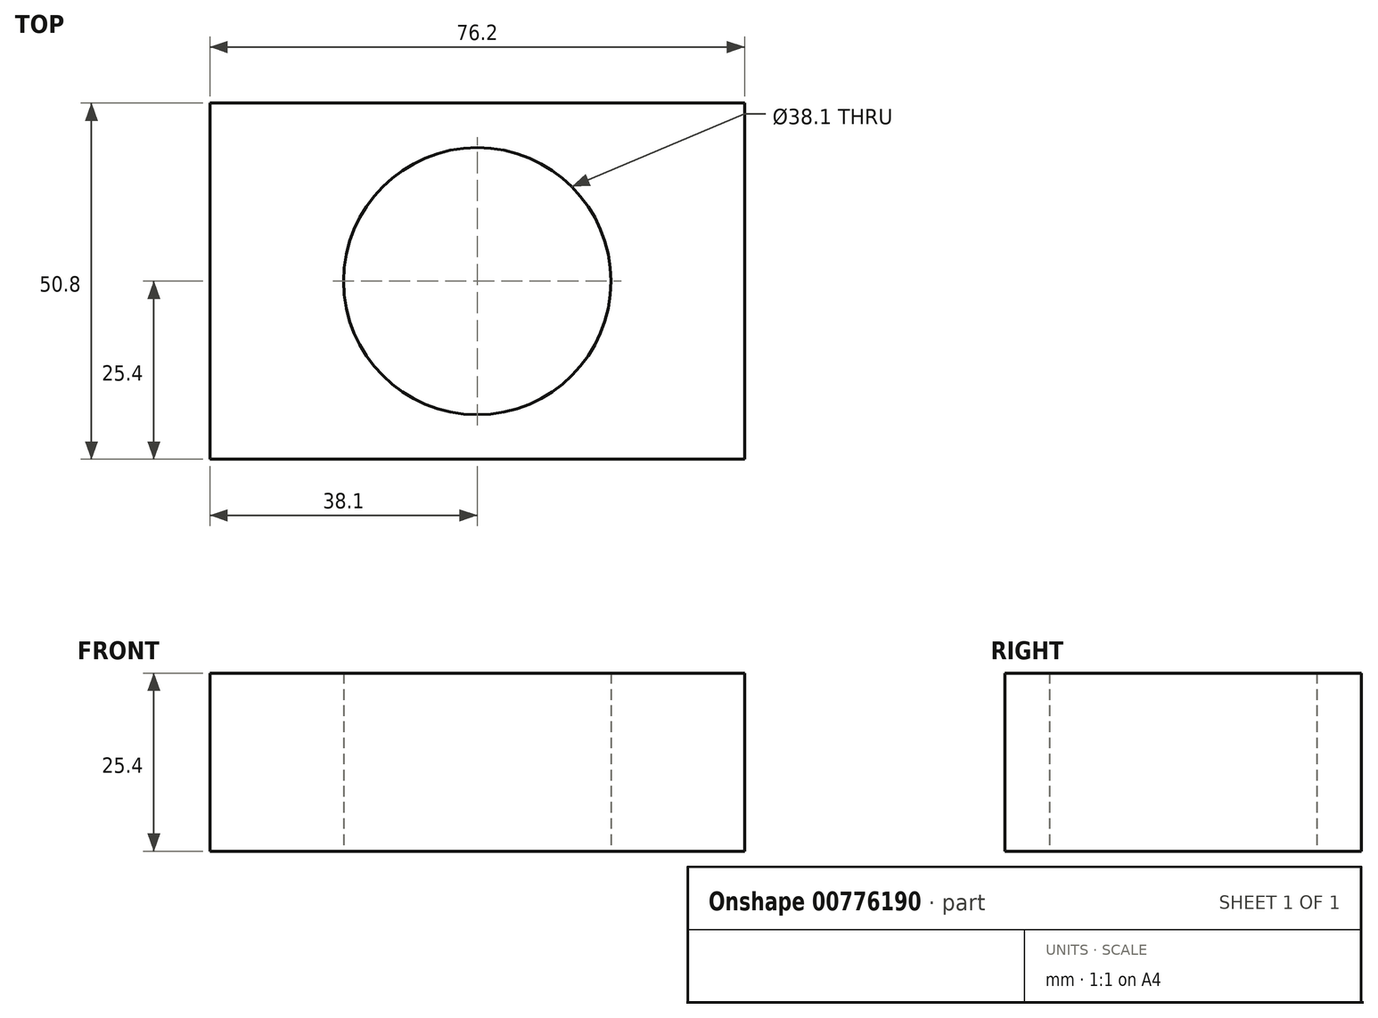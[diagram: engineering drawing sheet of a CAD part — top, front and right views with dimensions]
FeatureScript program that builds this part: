
annotation { "Feature Type Name" : "Feature", "Feature Type Description" : "" }
export const myFeature = defineFeature(function(context is Context, id is Id, definition is map)
    precondition{}
    {
        {
            var Q0;
            Q0=qCreatedBy(makeId("Top.planeOp"),FACE);
            var sketch = newSketch(context, id + "F0", { "sketchPlane" : qUnion([Q0])});
            skLineSegment(sketch, "E0.bottom", {"start": v(38.1, 25.4) * mm, "end": v(-38.1, 25.4) * mm});
            skLineSegment(sketch, "E0.top", {"start": v(38.1, -25.4) * mm, "end": v(-38.1, -25.4) * mm});
            skLineSegment(sketch, "E0.left", {"start": v(38.1, 25.4) * mm, "end": v(38.1, -25.4) * mm});
            skLineSegment(sketch, "E0.right", {"start": v(-38.1, 25.4) * mm, "end": v(-38.1, -25.4) * mm});
            skPoint(sketch, "E0.middle", {"position": v(0, 0) * mm});
            skCircle(sketch, "E1", {"center": v(0, 0) * mm, "radius": 19.05 * mm});
            skSolve(sketch);
        }
        {
            var Q0;
            Q0=makeQuery(id+"F0.imprint","IMPRINT",FACE,{"disambiguationData":[TD([[makeQuery(id+"F0.imprint","IMPRINT",EDGE,{"derivedFrom":sQuery(id+"F0.wireOp",EDGE,"E0.bottom")}),1.0]])]});
            extrude(context, id + "F1", {"entities" : qUnion([Q0]), "depth" : 25.4 * mm, "offsetDistance" : 25.4 * mm});
        }
    });
